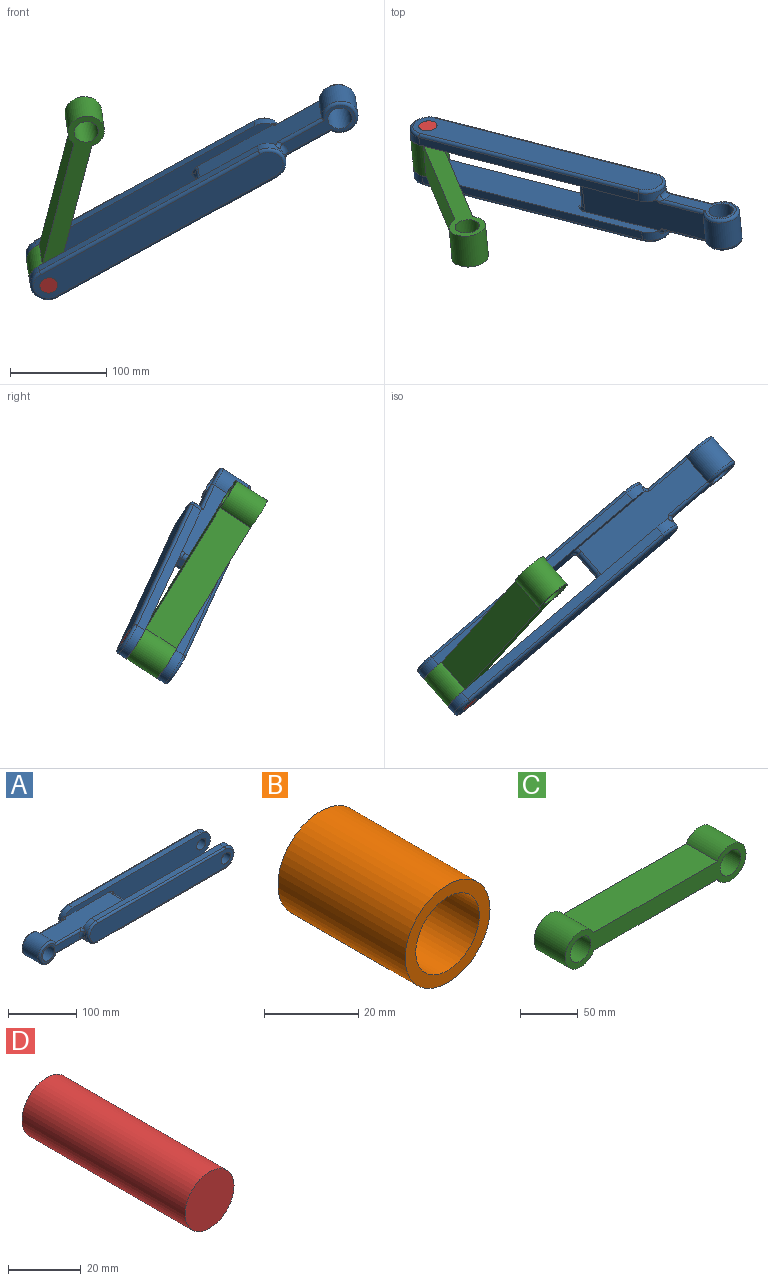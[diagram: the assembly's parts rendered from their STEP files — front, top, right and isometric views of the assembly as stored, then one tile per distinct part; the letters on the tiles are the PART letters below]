
ASSEMBLY  parts=4 mates=3
PART A: 49 faces, bbox 398.7x65.4x43.3 mm
  f0: plane 149.13x38.55mm, normal (0,0,1), area 5271.9mm2, adj f1,f11,f12,f31,f34,f35,f40,f46
  f1: cylinder r=19.05mm len=38.1mm, axis (0,1,0), area 3166.9mm2, adj f0,f2,f30,f33
  f2: plane 149.13x38.55mm, normal (0,0,-1), area 5270.7mm2, adj f1,f11,f12,f29,f32,f37,f38,f43
  f3: plane 27.94x8.89mm, normal (1,0,0), area 248.4mm2, adj f41,f42,f44,f47
  f4: cylinder r=12.7mm len=38.1mm, axis (0,1,0), area 3040.2mm2, adj f5,f6
  f5: plane 81.52x31.75mm, normal (0,-1,0), area 915.1mm2, adj f4,f32,f33,f34,f39
  f6: plane 81.47x31.75mm, normal (0,1,0), area 914.2mm2, adj f4,f29,f30,f31,f36
  f7: plane 266.7x9.53mm, normal (0,0,1), area 2540.3mm2, adj f8,f11,f20,f22
  f8: cylinder r=19.05mm len=38.1mm, axis (0,1,0), area 484.5mm2, adj f7,f9,f11,f24,f38,f39,f40
  f9: plane 266.65x9.53mm, normal (0,0,-1), area 2539.8mm2, adj f8,f11,f20,f23
  f10: plane 298.42x31.75mm, normal (0,-1,0), area 8972.8mm2, adj f18,f21,f22,f23,f24
  f11: plane 304.65x39.99mm, normal (0,1,0), area 9078mm2, adj f0,f2,f7,f8,f9,f18,f20,f38
  f12: plane 304.74x39.99mm, normal (0,-1,0), area 9077.7mm2, adj f0,f2,f13,f14,f15,f17,f19,f35
  f13: plane 266.73x9.53mm, normal (0,0,-1), area 2540.6mm2, adj f12,f14,f19,f25
  f14: cylinder r=19.05mm len=38.1mm, axis (0,-1,0), area 484.5mm2, adj f12,f13,f15,f26,f35,f36,f37
  f15: plane 266.67x9.53mm, normal (0,0,1), area 2540.1mm2, adj f12,f14,f19,f28
  f16: plane 298.45x31.75mm, normal (0,1,0), area 8973.7mm2, adj f17,f25,f26,f27,f28
  f17: cylinder r=9.54mm len=19.08mm, axis (0,-1,0), area 761.1mm2, adj f12,f16
  f18: cylinder r=9.54mm len=19.08mm, axis (0,-1,0), area 761.1mm2, adj f10,f11
  f19: cylinder r=19.05mm len=38.1mm, axis (0,1,0), area 570mm2, adj f12,f13,f15,f27
  f20: cylinder r=19.05mm len=38.1mm, axis (0,-1,0), area 570mm2, adj f7,f9,f11,f21
  f21: torus R=15.88mm, axis (0,-1,0), area 280.4mm2, adj f10,f20,f22,f23
  f22: cylinder r=3.17mm len=266.7mm, axis (1,0,0), area 1330.1mm2, adj f7,f10,f21,f24
  f23: cylinder r=3.17mm len=266.65mm, axis (-1,0,0), area 1329.9mm2, adj f9,f10,f21,f24
  f24: torus R=15.88mm, axis (0,-1,0), area 280.4mm2, adj f8,f10,f22,f23
  f25: cylinder r=3.17mm len=266.73mm, axis (1,0,0), area 1330.2mm2, adj f13,f16,f26,f27
  f26: torus R=15.88mm, axis (0,1,0), area 280.4mm2, adj f14,f16,f25,f28
  f27: torus R=15.88mm, axis (0,1,0), area 280.4mm2, adj f16,f19,f25,f28
  f28: cylinder r=3.17mm len=266.67mm, axis (-1,0,0), area 1330mm2, adj f15,f16,f26,f27
  f29: cylinder r=3.17mm len=55.21mm, axis (1,0,0), area 260.1mm2, adj f2,f6,f30,f37
  f30: torus R=15.88mm, axis (0,-1,0), area 477mm2, adj f1,f6,f29,f31
  f31: cylinder r=3.17mm len=54.94mm, axis (-1,0,0), area 259.2mm2, adj f0,f6,f30,f35
  f32: cylinder r=3.17mm len=55.21mm, axis (-1,0,0), area 260.2mm2, adj f2,f5,f33,f38
  f33: torus R=15.88mm, axis (0,-1,0), area 477mm2, adj f1,f5,f32,f34
  f34: cylinder r=3.17mm len=55.08mm, axis (1,0,0), area 259.8mm2, adj f0,f5,f33,f40
  f35: bspline ~9.32x8.13mm, area 40.6mm2, adj f0,f12,f14,f31,f36
  f36: torus R=24.13mm, axis (0,-1,0), area 88.8mm2, adj f6,f14,f35,f37
  f37: bspline ~9.32x8.25mm, area 40.9mm2, adj f2,f12,f14,f29,f36
  f38: bspline ~9.32x8.22mm, area 40.9mm2, adj f2,f8,f11,f32,f39
  f39: torus R=24.13mm, axis (0,-1,0), area 88.8mm2, adj f5,f8,f38,f40
  f40: bspline ~9.32x8.16mm, area 40.7mm2, adj f0,f8,f11,f34,f39
  f41: cylinder r=5.08mm len=8.89mm, axis (0,0,-1), area 70.9mm2, adj f3,f12,f43,f46
  f42: cylinder r=5.08mm len=8.89mm, axis (0,0,-1), area 70.9mm2, adj f3,f11,f45,f48
  f43: torus R=10.16mm, axis (0,0,1), area 54.2mm2, adj f2,f12,f41,f44
  f44: cylinder r=5.08mm len=27.94mm, axis (0,-1,0), area 223mm2, adj f2,f3,f43,f45
  f45: torus R=10.16mm, axis (0,0,1), area 54.2mm2, adj f2,f11,f42,f44
  f46: torus R=10.16mm, axis (0,0,1), area 54.2mm2, adj f0,f12,f41,f47
  f47: cylinder r=5.08mm len=27.94mm, axis (0,1,0), area 223mm2, adj f0,f3,f46,f48
  f48: torus R=10.16mm, axis (0,0,1), area 54.2mm2, adj f0,f11,f42,f47
PART B: 4 faces, bbox 25.4x38.1x25.4 mm
  f0: cylinder r=9.53mm len=38.1mm, axis (0,1,0), area 2280.2mm2, adj f2,f3
  f1: cylinder r=12.7mm len=38.1mm, axis (0,1,0), area 3040.2mm2, adj f2,f3
  f2: plane 25.4x25.4mm, normal (0,-1,0), area 221.7mm2, adj f0,f1
  f3: plane 25.4x25.4mm, normal (0,1,0), area 221.7mm2, adj f0,f1
PART C: 8 faces, bbox 222.3x38.1x38.1 mm
  f0: cylinder r=19.05mm len=38.1mm, axis (0,1,0), area 3800.3mm2, adj f1,f3,f6,f7
  f1: plane 151.15x38.1mm, normal (0,0,-1), area 5759mm2, adj f0,f2,f6,f7
  f2: cylinder r=19.05mm len=38.1mm, axis (0,1,0), area 3800.3mm2, adj f1,f3,f6,f7
  f3: plane 151.15x38.1mm, normal (0,0,1), area 5759mm2, adj f0,f2,f6,f7
  f4: cylinder r=12.7mm len=38.1mm, axis (0,1,0), area 3040.2mm2, adj f6,f7
  f5: cylinder r=12.7mm len=38.1mm, axis (0,1,0), area 3040.2mm2, adj f6,f7
  f6: plane 222.25x38.1mm, normal (0,-1,0), area 4080.5mm2, adj f0,f1,f2,f3,f4,f5
  f7: plane 222.25x38.1mm, normal (0,1,0), area 4080.5mm2, adj f0,f1,f2,f3,f4,f5
PART D: 3 faces, bbox 19.1x63.5x19.1 mm
  f0: cylinder r=9.53mm len=63.5mm, axis (0,1,0), area 3800.3mm2, adj f1,f2
  f1: plane 19.05x19.05mm, normal (0,1,0), area 285mm2, adj f0
  f2: plane 19.05x19.05mm, normal (0,-1,0), area 285mm2, adj f0
PLACE A rot(axis=(0.04,0.96,0.29),149.1deg) t=(-95.95,444.02,-363.39)mm
PLACE B rot(axis=(-0.16,0.27,-0.95),169.9deg) t=(-410.67,498.03,-565.62)mm
PLACE C rot(axis=(-0.62,-0.25,0.75),163.3deg) t=(-310.46,431.49,-446.82)mm
PLACE D rot(axis=(-0.81,0.13,-0.57),150.7deg) t=(-369.38,462.12,-527.02)mm
MATE revolute A.f17 <-> D.f0  axis (0.08,-0.84,-0.54) through (-340.08,526.11,-528.01)mm
MATE revolute C.f2 <-> B.f0  axis (0.08,-0.84,-0.54) through (-337.01,494.14,-548.51)mm
MATE revolute B.f0 <-> D.f0  axis (0.08,-0.84,-0.54) through (-338.54,510.12,-538.26)mm
